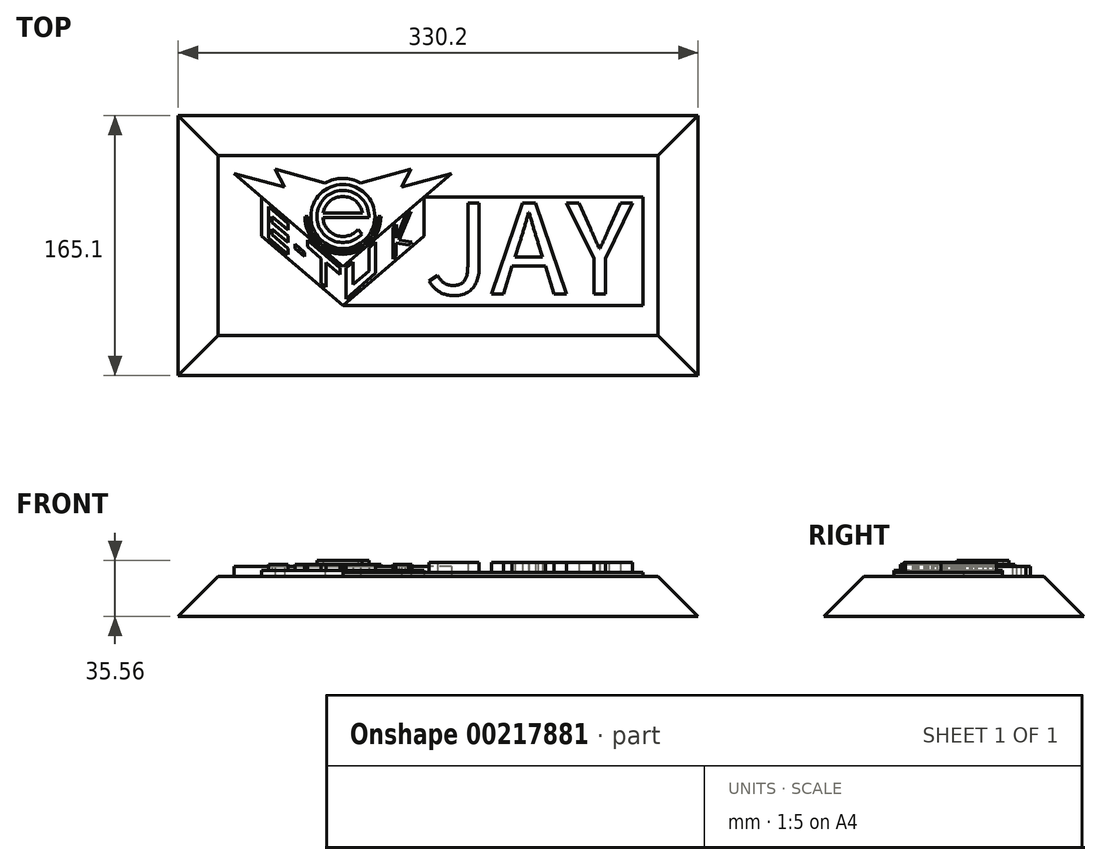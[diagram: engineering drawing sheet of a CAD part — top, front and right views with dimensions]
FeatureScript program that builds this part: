
annotation { "Feature Type Name" : "Feature", "Feature Type Description" : "" }
export const myFeature = defineFeature(function(context is Context, id is Id, definition is map)
    precondition{}
    {
        {
            var Q0;
            Q0=qCreatedBy(makeId("Top.planeOp"),FACE);
            var sketch = newSketch(context, id + "F0", { "sketchPlane" : qUnion([Q0])});
            skArc(sketch, "E0", {"start": v(12.53, 2.07) * mm, "mid": v(0, 12.7) * mm, "end": v(-12.53, 2.07) * mm});
            skArc(sketch, "E1", {"start": v(16.5, -0.78) * mm, "mid": v(-15.23, 6.37) * mm, "end": v(12.14, -11.18) * mm});
            skLineSegment(sketch, "E2", {"start": v(12.7, -0.78) * mm, "end": v(-12.68, -0.78) * mm});
            skLineSegment(sketch, "E3", {"start": v(-12.68, -0.78) * mm, "end": v(16.5, -0.78) * mm});
            skLineSegment(sketch, "E4", {"start": v(9.59, -8.33) * mm, "end": v(12.14, -11.18) * mm});
            skArc(sketch, "E5.trimOffspring", {"start": v(-12.68, -0.78) * mm, "mid": v(-4.08, -12.03) * mm, "end": v(9.59, -8.33) * mm});
            skLineSegment(sketch, "E6", {"start": v(-12.53, 2.07) * mm, "end": v(12.53, 2.07) * mm});
            skSolve(sketch);
        }
        {
            var Q0;
            Q0=makeQuery(id+"F0.imprint","IMPRINT",FACE,{"disambiguationData":[TD([[makeQuery(id+"F0.imprint","IMPRINT",EDGE,{"derivedFrom":sQuery(id+"F0.wireOp",EDGE,"E0")}),-1.0]])]});
            extrude(context, id + "F1", {"entities" : qUnion([Q0]), "depth" : 10.16 * mm});
        }
        {
            var Q0;
            Q0=qCreatedBy(makeId("Top.planeOp"),FACE);
            var sketch = newSketch(context, id + "F2", { "sketchPlane" : qUnion([Q0])});
            skCircle(sketch, "E7", {"center": v(0, 0) * mm, "radius": 20.32 * mm});
            skSolve(sketch);
        }
        {
            var Q0;
            Q0=qSketchRegion(id+"F2",true);
            extrude(context, id + "F3", {"entities" : qUnion([Q0]), "operationType" : NewBodyOperationType.ADD, "depth" : 7.62 * mm});
        }
        {
            var Q0;
            Q0=qCreatedBy(makeId("Top.planeOp"),FACE);
            var sketch = newSketch(context, id + "F4", { "sketchPlane" : qUnion([Q0])});
            skLineSegment(sketch, "E8", {"start": v(-69.02, 27.27) * mm, "end": v(-37.13, 18.72) * mm});
            skLineSegment(sketch, "E9", {"start": v(-37.13, 18.72) * mm, "end": v(-43.14, 30.14) * mm});
            skLineSegment(sketch, "E10", {"start": v(-43.14, 30.14) * mm, "end": v(-11.32, 21.31) * mm});
            skLineSegment(sketch, "E11", {"start": v(-69.02, 27.27) * mm, "end": v(0, -31.75) * mm});
            skLineSegment(sketch, "E12.MirrorCS", {"start": v(43.14, 30.14) * mm, "end": v(11.32, 21.31) * mm});
            skLineSegment(sketch, "E13.MirrorCS", {"start": v(69.02, 27.27) * mm, "end": v(0, -31.75) * mm});
            skLineSegment(sketch, "E14.MirrorCS", {"start": v(69.02, 27.27) * mm, "end": v(37.13, 18.72) * mm});
            skLineSegment(sketch, "E15.MirrorCS", {"start": v(37.13, 18.72) * mm, "end": v(43.14, 30.14) * mm});
            skArc(sketch, "E16.trimOffspring", {"start": v(11.32, 21.31) * mm, "mid": v(0, 24.13) * mm, "end": v(-11.32, 21.31) * mm});
            skSolve(sketch);
        }
        {
            var Q0;
            Q0=qSketchRegion(id+"F4",true);
            var Q1;
            Q1=makeQuery(id+"F2.imprint","IMPRINT",FACE,{"disambiguationData":[TD([[makeQuery(id+"F2.imprint","IMPRINT",EDGE,{"derivedFrom":sQuery(id+"F2.wireOp",EDGE,"E7")}),1.0]])]});
            extrude(context, id + "F5", {"entities" : qUnion([Q0, Q1]), "operationType" : NewBodyOperationType.ADD, "depth" : 6.35 * mm});
        }
        {
            var Q0;
            Q0=qCreatedBy(makeId("Top.planeOp"),FACE);
            var sketch = newSketch(context, id + "F6", { "sketchPlane" : qUnion([Q0])});
            skLineSegment(sketch, "E17", {"start": v(-51.6, -12.38) * mm, "end": v(0, -56.51) * mm});
            skLineSegment(sketch, "E18", {"start": v(0, -56.51) * mm, "end": v(51.6, -12.38) * mm});
            skLineSegment(sketch, "E19", {"start": v(-51.6, 12.38) * mm, "end": v(-51.6, -12.38) * mm});
            skLineSegment(sketch, "E20", {"start": v(51.6, 12.38) * mm, "end": v(51.6, -12.38) * mm});
            skLineSegment(sketch, "E21", {"start": v(-51.6, 12.38) * mm, "end": v(0, -31.75) * mm});
            skLineSegment(sketch, "E22", {"start": v(0, -31.75) * mm, "end": v(51.6, 12.38) * mm});
            skSolve(sketch);
        }
        {
            var Q0;
            Q0=qSketchRegion(id+"F6",true);
            extrude(context, id + "F7", {"entities" : qUnion([Q0]), "operationType" : NewBodyOperationType.ADD, "depth" : 3.8 * mm});
        }
        {
            var Q0;
            Q0=makeQuery(id+"F7.opExtrude","CAP_FACE",FACE,{"disambiguationData":[OSD([sQuery(id+"F6.wireOp",EDGE,"E17"),sQuery(id+"F6.wireOp",EDGE,"E18"),sQuery(id+"F6.wireOp",EDGE,"E19"),sQuery(id+"F6.wireOp",EDGE,"E20"),sQuery(id+"F6.wireOp",EDGE,"E21"),sQuery(id+"F6.wireOp",EDGE,"E22")])],"isStart":false});
            var sketch = newSketch(context, id + "F8", { "sketchPlane" : qUnion([Q0])});
            skPoint(sketch, "E23.startSnap0", {"position": v(-51.6, 0) * mm});
            skLineSegment(sketch, "E24", {"start": v(-51.6, -9.87) * mm, "end": v(-51.6, 9.87) * mm, "construction": true});
            skLineSegment(sketch, "E25", {"start": v(-47.26, 6.16) * mm, "end": v(-34.74, -4.55) * mm});
            skLineSegment(sketch, "E26", {"start": v(-34.74, -4.55) * mm, "end": v(-34.74, -8.63) * mm});
            skLineSegment(sketch, "E27", {"start": v(-34.74, -8.63) * mm, "end": v(-44.83, 0) * mm});
            skLineSegment(sketch, "E28", {"start": v(-44.83, 0) * mm, "end": v(-44.83, -3.75) * mm});
            skLineSegment(sketch, "E29", {"start": v(-44.83, -3.75) * mm, "end": v(-34.74, -12.38) * mm});
            skLineSegment(sketch, "E30", {"start": v(-34.74, -12.38) * mm, "end": v(-34.74, -16.46) * mm});
            skLineSegment(sketch, "E31", {"start": v(-34.74, -16.46) * mm, "end": v(-44.83, -7.83) * mm});
            skLineSegment(sketch, "E32", {"start": v(-44.83, -7.83) * mm, "end": v(-44.83, -11.58) * mm});
            skLineSegment(sketch, "E33", {"start": v(-44.83, -11.58) * mm, "end": v(-34.74, -20.21) * mm});
            skLineSegment(sketch, "E34", {"start": v(-34.74, -20.21) * mm, "end": v(-34.74, -24.3) * mm});
            skLineSegment(sketch, "E35", {"start": v(-34.74, -24.3) * mm, "end": v(-47.26, -13.59) * mm});
            skLineSegment(sketch, "E36", {"start": v(-47.26, 6.16) * mm, "end": v(-47.26, -13.59) * mm});
            skLineSegment(sketch, "E37", {"start": v(-30.38, -20.21) * mm, "end": v(-30.38, -17.65) * mm});
            skLineSegment(sketch, "E38", {"start": v(-30.38, -17.65) * mm, "end": v(-24.17, -22.96) * mm});
            skLineSegment(sketch, "E39", {"start": v(-24.17, -22.96) * mm, "end": v(-24.17, -25.53) * mm});
            skLineSegment(sketch, "E40", {"start": v(-24.17, -25.53) * mm, "end": v(-30.38, -20.21) * mm});
            skLineSegment(sketch, "E41", {"start": v(-22.38, -15.12) * mm, "end": v(-1.9, -32.63) * mm});
            skLineSegment(sketch, "E42", {"start": v(-1.9, -32.63) * mm, "end": v(-1.9, -36.71) * mm});
            skLineSegment(sketch, "E43", {"start": v(-1.9, -36.71) * mm, "end": v(-10.6, -29.28) * mm});
            skLineSegment(sketch, "E44", {"start": v(-10.6, -29.28) * mm, "end": v(-10.6, -44.95) * mm});
            skLineSegment(sketch, "E45", {"start": v(-10.6, -44.95) * mm, "end": v(-13.7, -42.3) * mm});
            skLineSegment(sketch, "E46", {"start": v(-13.7, -42.3) * mm, "end": v(-13.7, -26.63) * mm});
            skLineSegment(sketch, "E47", {"start": v(-13.7, -26.63) * mm, "end": v(-22.38, -19.2) * mm});
            skLineSegment(sketch, "E48", {"start": v(-22.38, -19.2) * mm, "end": v(-22.38, -15.12) * mm});
            skLineSegment(sketch, "E49", {"start": v(1.9, -32.62) * mm, "end": v(6.3, -28.86) * mm});
            skLineSegment(sketch, "E50", {"start": v(6.3, -28.86) * mm, "end": v(6.3, -43.26) * mm});
            skLineSegment(sketch, "E51", {"start": v(6.3, -43.26) * mm, "end": v(16.5, -34.54) * mm});
            skLineSegment(sketch, "E52", {"start": v(16.5, -34.54) * mm, "end": v(16.5, -20.14) * mm});
            skLineSegment(sketch, "E53", {"start": v(16.5, -20.14) * mm, "end": v(20.85, -16.3) * mm});
            skLineSegment(sketch, "E54", {"start": v(20.85, -16.3) * mm, "end": v(20.85, -36.06) * mm});
            skLineSegment(sketch, "E55", {"start": v(20.85, -36.06) * mm, "end": v(1.9, -52.37) * mm});
            skLineSegment(sketch, "E56", {"start": v(1.9, -52.37) * mm, "end": v(1.9, -32.62) * mm});
            skLineSegment(sketch, "E57", {"start": v(31.73, -7.12) * mm, "end": v(31.73, -27.15) * mm});
            skLineSegment(sketch, "E58", {"start": v(31.73, -27.15) * mm, "end": v(33.91, -25.22) * mm});
            skLineSegment(sketch, "E59", {"start": v(33.91, -25.22) * mm, "end": v(33.91, -16.82) * mm});
            skLineSegment(sketch, "E60", {"start": v(33.94, -13.64) * mm, "end": v(33.94, -5.23) * mm});
            skLineSegment(sketch, "E61", {"start": v(33.94, -5.23) * mm, "end": v(31.73, -7.12) * mm});
            skLineSegment(sketch, "E62", {"start": v(41.79, -18.27) * mm, "end": v(44, -16.38) * mm});
            skLineSegment(sketch, "E63", {"start": v(33.94, -13.64) * mm, "end": v(39.5, 0) * mm});
            skLineSegment(sketch, "E64", {"start": v(33.91, -16.82) * mm, "end": v(41.79, -18.27) * mm});
            skLineSegment(sketch, "E65", {"start": v(44, -16.38) * mm, "end": v(35.85, -14.87) * mm});
            skLineSegment(sketch, "E66", {"start": v(35.85, -14.87) * mm, "end": v(43.2, 3.16) * mm});
            skLineSegment(sketch, "E67", {"start": v(39.5, 0) * mm, "end": v(43.2, 3.16) * mm});
            skSolve(sketch);
        }
        {
            var Q0;
            Q0=qSketchRegion(id+"F8",true);
            extrude(context, id + "F9", {"entities" : qUnion([Q0]), "operationType" : NewBodyOperationType.ADD, "depth" : 3.8 * mm});
        }
        {
            var Q0;
            Q0=makeQuery(id+"F5.boolean.opBoolean","MERGE",FACE,{"derivedFrom":[makeQuery(id+"F5.opExtrude","CAP_FACE",FACE,{"disambiguationData":[OSD([sQuery(id+"F2.wireOp",EDGE,"E7")])],"isStart":false}),makeQuery(id+"F5.opExtrude","CAP_FACE",FACE,{"disambiguationData":[OSD([sQuery(id+"F4.wireOp",EDGE,"E8"),sQuery(id+"F4.wireOp",EDGE,"E9"),sQuery(id+"F4.wireOp",EDGE,"E10"),sQuery(id+"F4.wireOp",EDGE,"E11"),sQuery(id+"F4.wireOp",EDGE,"E13.MirrorCS"),sQuery(id+"F4.wireOp",EDGE,"E14.MirrorCS"),sQuery(id+"F4.wireOp",EDGE,"E12.MirrorCS"),sQuery(id+"F4.wireOp",EDGE,"E15.MirrorCS"),sQuery(id+"F4.wireOp",EDGE,"E16.trimOffspring")])],"isStart":false})]});
            var sketch = newSketch(context, id + "F10", { "sketchPlane" : qUnion([Q0])});
            skArc(sketch, "E68", {"start": v(-24.13, 0) * mm, "mid": v(0, -24.13) * mm, "end": v(24.13, 0) * mm});
            skArc(sketch, "E69", {"start": v(-22.23, 0) * mm, "mid": v(0, -22.23) * mm, "end": v(22.23, 0) * mm});
            skLineSegment(sketch, "E70", {"start": v(-24.13, 0) * mm, "end": v(-22.23, 0) * mm});
            skLineSegment(sketch, "E71", {"start": v(24.13, 0) * mm, "end": v(22.23, 0) * mm});
            skSolve(sketch);
        }
        {
            var Q0;
            Q0=qSketchRegion(id+"F10",true);
            extrude(context, id + "F11", {"entities" : qUnion([Q0]), "operationType" : NewBodyOperationType.ADD, "depth" : 1.27 * mm});
        }
        {
            var Q0;
            {var subQ0=sQuery(id+"F2.wireOp",EDGE,"E7");Q0=makeQuery(id+"F7.boolean.opBoolean","MERGE",FACE,{"derivedFrom":[makeQuery(id+"F5.boolean.opBoolean","MERGE",FACE,{"derivedFrom":[makeQuery(id+"F3.boolean.opBoolean","MERGE",FACE,{"derivedFrom":[makeQuery(id+"F1.opExtrude","CAP_FACE",FACE,{"disambiguationData":[OSD([sQuery(id+"F0.wireOp",EDGE,"E0"),sQuery(id+"F0.wireOp",EDGE,"E1"),sQuery(id+"F0.wireOp",EDGE,"E3"),sQuery(id+"F0.wireOp",EDGE,"E4"),sQuery(id+"F0.wireOp",EDGE,"E5.trimOffspring"),sQuery(id+"F0.wireOp",EDGE,"E6")])],"isStart":true}),makeQuery(id+"F3.opExtrude","CAP_FACE",FACE,{"disambiguationData":[OSD([subQ0])],"isStart":true})]}),makeQuery(id+"F5.opExtrude","CAP_FACE",FACE,{"disambiguationData":[OSD([subQ0])],"isStart":true}),makeQuery(id+"F5.opExtrude","CAP_FACE",FACE,{"disambiguationData":[OSD([sQuery(id+"F4.wireOp",EDGE,"E8"),sQuery(id+"F4.wireOp",EDGE,"E9"),sQuery(id+"F4.wireOp",EDGE,"E10"),sQuery(id+"F4.wireOp",EDGE,"E11"),sQuery(id+"F4.wireOp",EDGE,"E13.MirrorCS"),sQuery(id+"F4.wireOp",EDGE,"E14.MirrorCS"),sQuery(id+"F4.wireOp",EDGE,"E12.MirrorCS"),sQuery(id+"F4.wireOp",EDGE,"E15.MirrorCS"),sQuery(id+"F4.wireOp",EDGE,"E16.trimOffspring")])],"isStart":true})]}),makeQuery(id+"F7.opExtrude","CAP_FACE",FACE,{"disambiguationData":[OSD([sQuery(id+"F6.wireOp",EDGE,"E17"),sQuery(id+"F6.wireOp",EDGE,"E18"),sQuery(id+"F6.wireOp",EDGE,"E19"),sQuery(id+"F6.wireOp",EDGE,"E20"),sQuery(id+"F6.wireOp",EDGE,"E21"),sQuery(id+"F6.wireOp",EDGE,"E22")])],"isStart":true})]});}
            var sketch = newSketch(context, id + "F12", { "sketchPlane" : qUnion([Q0])});
            skLineSegment(sketch, "E72.bottom", {"start": v(0, 56.51) * mm, "end": v(190.5, 56.51) * mm});
            skLineSegment(sketch, "E72.right", {"start": v(190.5, 56.51) * mm, "end": v(190.5, -12.38) * mm});
            skLineSegment(sketch, "E73", {"start": v(51.6, -12.38) * mm, "end": v(190.5, -12.38) * mm});
            skLineSegment(sketch, "E74", {"start": v(0, 56.51) * mm, "end": v(51.6, 12.38) * mm});
            skLineSegment(sketch, "E75", {"start": v(51.6, 12.38) * mm, "end": v(51.6, -12.38) * mm});
            skSolve(sketch);
        }
        {
            var Q0;
            Q0 = qSketchRegion(id + "F12", true);
            extrude(context, id + "F13", {"entities" : qUnion([Q0]), "operationType" : NewBodyOperationType.ADD, "oppositeDirection" : true, "depth" : 2.54 * mm});
        }
        {
            var Q0;
            Q0=makeQuery(id+"F13.opExtrude","CAP_FACE",FACE,{"disambiguationData":[OSD([sQuery(id+"F12.wireOp",EDGE,"E72.bottom"),sQuery(id+"F12.wireOp",EDGE,"E72.right"),sQuery(id+"F12.wireOp",EDGE,"E73"),sQuery(id+"F12.wireOp",EDGE,"E74"),sQuery(id+"F12.wireOp",EDGE,"E75")])],"isStart":false});
            var sketch = newSketch(context, id + "F14", { "sketchPlane" : qUnion([Q0])});
            skText(sketch, "E76", { "text": "JAY", "fontName": "NotoSansCJKkr-Regular.otf"});
            const initialGuessF14  = {"E76": [0.05209, -0.0492, 1, 0, 0.05672]};
            skSetInitialGuess(sketch, initialGuessF14);
            skSolve(sketch);
        }
        {
            var Q0;
            Q0 = qSketchRegion(id + "F14", true);
            extrude(context, id + "F15", {"entities" : qUnion([Q0]), "operationType" : NewBodyOperationType.ADD, "depth" : 6.35 * mm});
        }
        {
            var Q0;
            {var subQ0=sQuery(id+"F2.wireOp",EDGE,"E7");Q0=makeQuery(id+"F13.boolean.opBoolean","MERGE",FACE,{"derivedFrom":[makeQuery(id+"F7.boolean.opBoolean","MERGE",FACE,{"derivedFrom":[makeQuery(id+"F5.boolean.opBoolean","MERGE",FACE,{"derivedFrom":[makeQuery(id+"F3.boolean.opBoolean","MERGE",FACE,{"derivedFrom":[makeQuery(id+"F1.opExtrude","CAP_FACE",FACE,{"disambiguationData":[OSD([sQuery(id+"F0.wireOp",EDGE,"E0"),sQuery(id+"F0.wireOp",EDGE,"E1"),sQuery(id+"F0.wireOp",EDGE,"E3"),sQuery(id+"F0.wireOp",EDGE,"E4"),sQuery(id+"F0.wireOp",EDGE,"E5.trimOffspring"),sQuery(id+"F0.wireOp",EDGE,"E6")])],"isStart":true}),makeQuery(id+"F3.opExtrude","CAP_FACE",FACE,{"disambiguationData":[OSD([subQ0])],"isStart":true})]}),makeQuery(id+"F5.opExtrude","CAP_FACE",FACE,{"disambiguationData":[OSD([subQ0])],"isStart":true}),makeQuery(id+"F5.opExtrude","CAP_FACE",FACE,{"disambiguationData":[OSD([sQuery(id+"F4.wireOp",EDGE,"E8"),sQuery(id+"F4.wireOp",EDGE,"E9"),sQuery(id+"F4.wireOp",EDGE,"E10"),sQuery(id+"F4.wireOp",EDGE,"E11"),sQuery(id+"F4.wireOp",EDGE,"E13.MirrorCS"),sQuery(id+"F4.wireOp",EDGE,"E14.MirrorCS"),sQuery(id+"F4.wireOp",EDGE,"E12.MirrorCS"),sQuery(id+"F4.wireOp",EDGE,"E15.MirrorCS"),sQuery(id+"F4.wireOp",EDGE,"E16.trimOffspring")])],"isStart":true})]}),makeQuery(id+"F7.opExtrude","CAP_FACE",FACE,{"disambiguationData":[OSD([sQuery(id+"F6.wireOp",EDGE,"E17"),sQuery(id+"F6.wireOp",EDGE,"E18"),sQuery(id+"F6.wireOp",EDGE,"E19"),sQuery(id+"F6.wireOp",EDGE,"E20"),sQuery(id+"F6.wireOp",EDGE,"E21"),sQuery(id+"F6.wireOp",EDGE,"E22")])],"isStart":true})]}),makeQuery(id+"F13.opExtrude","CAP_FACE",FACE,{"disambiguationData":[OSD([sQuery(id+"F12.wireOp",EDGE,"E72.bottom"),sQuery(id+"F12.wireOp",EDGE,"E72.right"),sQuery(id+"F12.wireOp",EDGE,"E73"),sQuery(id+"F12.wireOp",EDGE,"E74"),sQuery(id+"F12.wireOp",EDGE,"E75")])],"isStart":true})]});}
            var sketch = newSketch(context, id + "F16", { "sketchPlane" : qUnion([Q0])});
            skLineSegment(sketch, "E77.bottom", {"start": v(-79.18, -38.74) * mm, "end": v(200.22, -38.74) * mm});
            skLineSegment(sketch, "E77.top", {"start": v(-79.18, 75.56) * mm, "end": v(200.22, 75.56) * mm});
            skLineSegment(sketch, "E77.left", {"start": v(-79.18, -38.74) * mm, "end": v(-79.18, 75.56) * mm});
            skLineSegment(sketch, "E77.right", {"start": v(200.22, -38.74) * mm, "end": v(200.22, 75.56) * mm});
            skSolve(sketch);
        }
        {
            var Q0;
            Q0 = qSketchRegion(id + "F16", true);
            extrude(context, id + "F17", {"entities" : qUnion([Q0]), "operationType" : NewBodyOperationType.ADD, "depth" : 25.4 * mm, "hasDraft" : true, "draftAngle" : 45 * degree});
        }
    });
